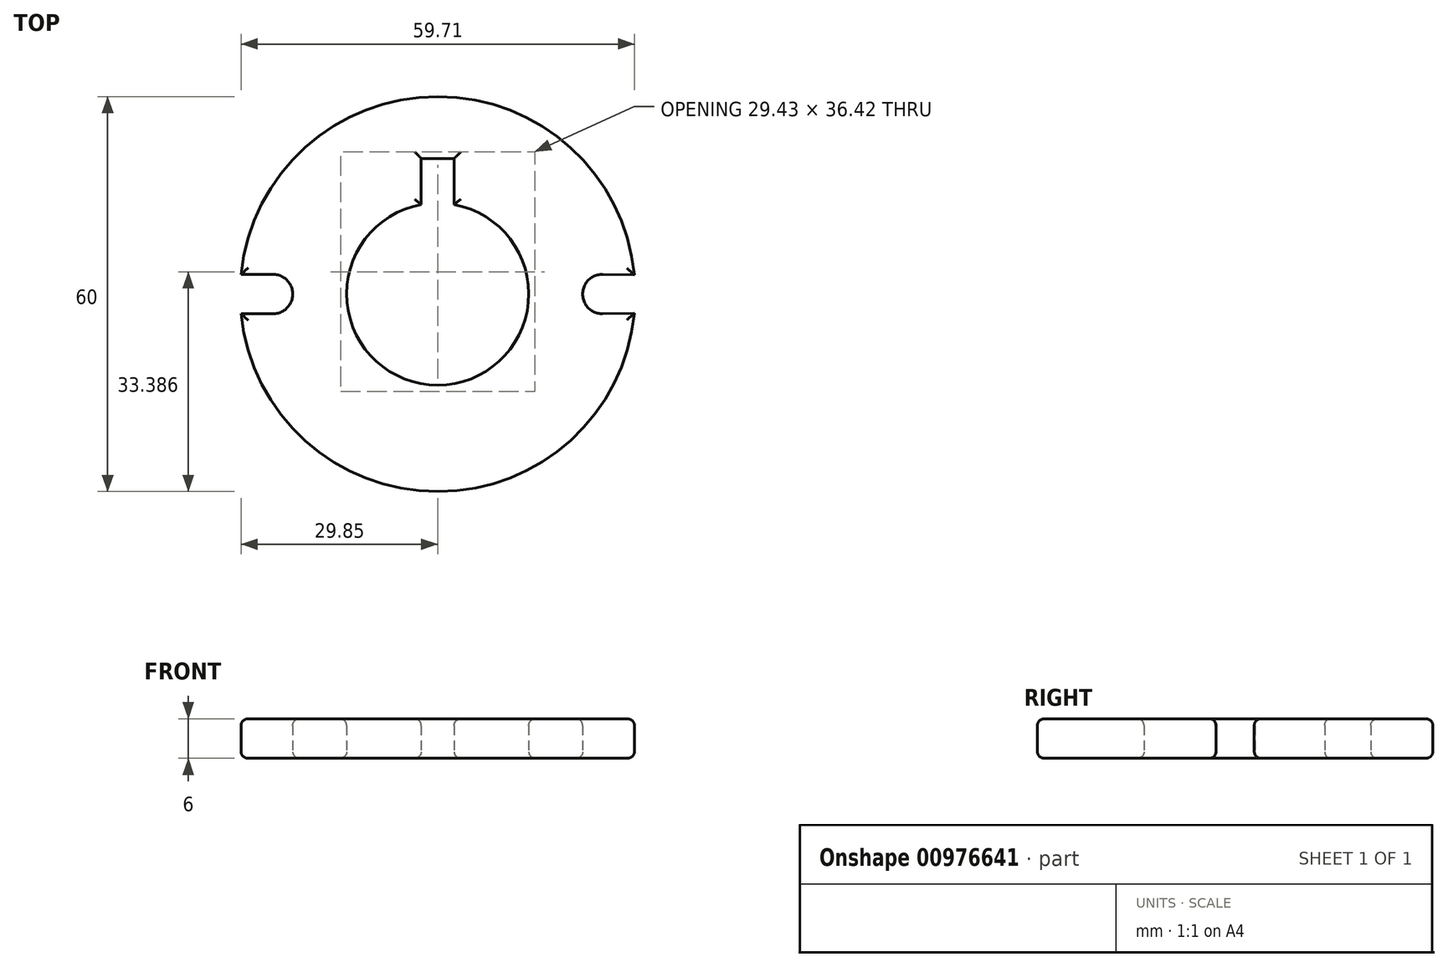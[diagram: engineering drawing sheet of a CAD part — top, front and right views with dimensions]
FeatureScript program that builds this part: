
annotation { "Feature Type Name" : "Feature", "Feature Type Description" : "" }
export const myFeature = defineFeature(function(context is Context, id is Id, definition is map)
    precondition{}
    {
        {
            var Q0;
            Q0=qCreatedBy(makeId("Top.planeOp"),FACE);
            var sketch = newSketch(context, id + "F0", { "sketchPlane" : qUnion([Q0])});
            skCircle(sketch, "E0", {"center": v(0, 0) * mm, "radius": 30 * mm});
            skCircle(sketch, "E1", {"center": v(0, 0) * mm, "radius": 13.82 * mm});
            skCircle(sketch, "E2", {"center": v(25, 0) * mm, "radius": 3 * mm});
            skLineSegment(sketch, "E3", {"start": v(25.06, 3) * mm, "end": v(29.86, 2.9) * mm});
            skLineSegment(sketch, "E4", {"start": v(25.06, -3) * mm, "end": v(29.86, -2.9) * mm});
            skLineSegment(sketch, "E5", {"start": v(0, 20.6) * mm, "end": v(-2.5, 20.6) * mm});
            skLineSegment(sketch, "E6", {"start": v(-2.5, 20.6) * mm, "end": v(-2.5, 13.6) * mm});
            skLineSegment(sketch, "E7", {"start": v(0, 20.6) * mm, "end": v(2.5, 20.6) * mm});
            skLineSegment(sketch, "E8", {"start": v(2.5, 20.6) * mm, "end": v(2.5, 13.6) * mm});
            skCircle(sketch, "E9.1.0", {"center": v(-25, 0) * mm, "radius": 3 * mm});
            skLineSegment(sketch, "E10", {"start": v(-25.02, 3) * mm, "end": v(-29.85, 3) * mm});
            skLineSegment(sketch, "E11", {"start": v(-25.01, -3) * mm, "end": v(-29.85, -3) * mm});
            skSolve(sketch);
        }
        {
            var Q0;
            {var subQ1=sQuery(id+"F0.wireOp",EDGE,"E3");Q0=makeQuery(id+"F0.imprint","IMPRINT",FACE,{"disambiguationData":[TD([[makeQuery(id+"F0.imprint","IMPRINT",EDGE,{"derivedFrom":subQ1}),1.0]])]});}
            extrude(context, id + "F1", {"entities" : qUnion([Q0]), "depth" : 6 * mm, "offsetDistance" : 25 * mm});
        }
        {
            var Q0;
            Q0=makeQuery(id+"F1.opExtrude","CAP_FACE",FACE,{"disambiguationData":[OSD([sQuery(id+"F0.wireOp",EDGE,"E0"),sQuery(id+"F0.wireOp",EDGE,"E1"),sQuery(id+"F0.wireOp",EDGE,"E2"),sQuery(id+"F0.wireOp",EDGE,"E3"),sQuery(id+"F0.wireOp",EDGE,"E4"),sQuery(id+"F0.wireOp",EDGE,"E5"),sQuery(id+"F0.wireOp",EDGE,"E6"),sQuery(id+"F0.wireOp",EDGE,"E7"),sQuery(id+"F0.wireOp",EDGE,"E8"),sQuery(id+"F0.wireOp",EDGE,"E9.1.0"),sQuery(id+"F0.wireOp",EDGE,"E10"),sQuery(id+"F0.wireOp",EDGE,"E11")])],"isStart":false});
            var Q1;
            Q1=makeQuery(id+"F1.opExtrude","CAP_FACE",FACE,{"disambiguationData":[OSD([sQuery(id+"F0.wireOp",EDGE,"E0"),sQuery(id+"F0.wireOp",EDGE,"E1"),sQuery(id+"F0.wireOp",EDGE,"E2"),sQuery(id+"F0.wireOp",EDGE,"E3"),sQuery(id+"F0.wireOp",EDGE,"E4"),sQuery(id+"F0.wireOp",EDGE,"E5"),sQuery(id+"F0.wireOp",EDGE,"E6"),sQuery(id+"F0.wireOp",EDGE,"E7"),sQuery(id+"F0.wireOp",EDGE,"E8"),sQuery(id+"F0.wireOp",EDGE,"E9.1.0"),sQuery(id+"F0.wireOp",EDGE,"E10"),sQuery(id+"F0.wireOp",EDGE,"E11")])],"isStart":true});
            fillet(context, id + "F2", {"entities" : qUnion([Q0, Q1]), "radius" : 1 * mm, "tangentPropagation" : true, "allowEdgeOverflow" : false});
        }
    });
